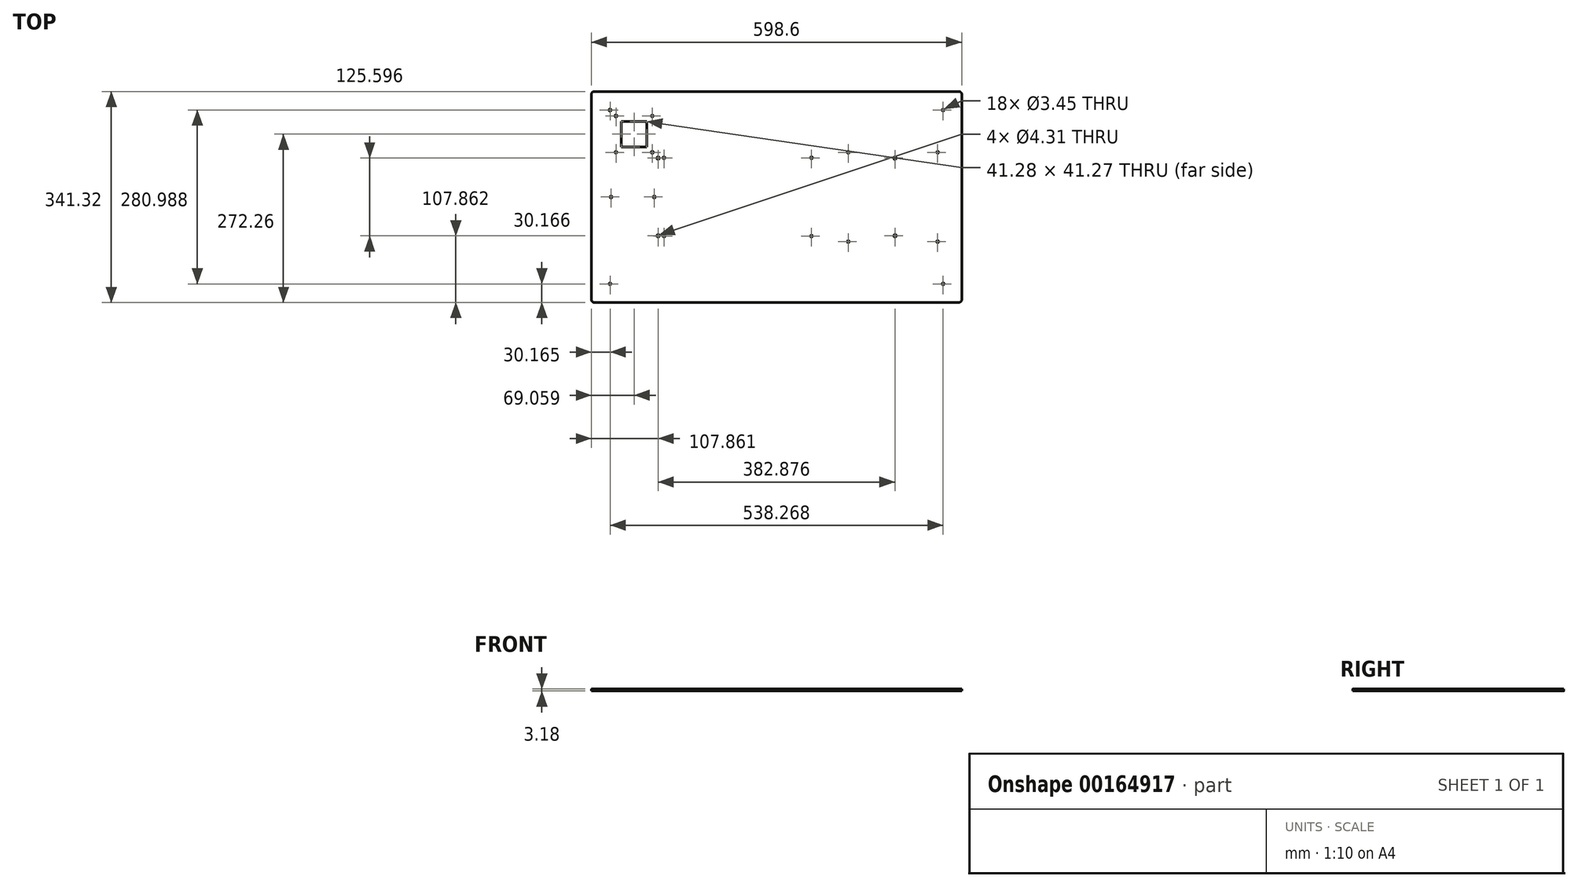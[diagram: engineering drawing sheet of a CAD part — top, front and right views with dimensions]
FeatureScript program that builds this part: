
annotation { "Feature Type Name" : "Feature", "Feature Type Description" : "" }
export const myFeature = defineFeature(function(context is Context, id is Id, definition is map)
    precondition{}
    {
        {
            var Q0;
            Q0=qCreatedBy(makeId("Top.planeOp"),FACE);
            var sketch = newSketch(context, id + "F0", { "sketchPlane" : qUnion([Q0])});
            skPoint(sketch, "E0.middle", {"position": v(0, 0) * mm});
            skLineSegment(sketch, "E1", {"start": v(0, 101.6) * mm, "end": v(0, 0) * mm, "construction": true});
            skLineSegment(sketch, "E2", {"start": v(0, 101.6) * mm, "end": v(-167.48, 101.6) * mm, "construction": true});
            skLineSegment(sketch, "E3.bottom", {"start": v(-138.11, 72.23) * mm, "end": v(-196.85, 72.23) * mm, "construction": true});
            skLineSegment(sketch, "E3.top", {"start": v(-138.11, 130.97) * mm, "end": v(-196.85, 130.97) * mm, "construction": true});
            skLineSegment(sketch, "E3.left", {"start": v(-138.11, 72.23) * mm, "end": v(-138.11, 130.97) * mm, "construction": true});
            skLineSegment(sketch, "E3.right", {"start": v(-196.85, 72.23) * mm, "end": v(-196.85, 130.97) * mm, "construction": true});
            skPoint(sketch, "E3.middle", {"position": v(-167.48, 101.6) * mm});
            skCircle(sketch, "E4", {"center": v(-196.85, 130.97) * mm, "radius": 1.73 * mm});
            skCircle(sketch, "E5", {"center": v(-138.11, 130.97) * mm, "radius": 1.73 * mm});
            skCircle(sketch, "E6", {"center": v(-138.11, 72.23) * mm, "radius": 1.73 * mm});
            skCircle(sketch, "E7", {"center": v(-196.85, 72.23) * mm, "radius": 1.73 * mm});
            skLineSegment(sketch, "E8", {"start": v(0, 0) * mm, "end": v(-119.17, 63.3) * mm, "construction": true});
            skLineSegment(sketch, "E9", {"start": v(0, 0) * mm, "end": v(-119.17, 0) * mm, "construction": true});
            skLineSegment(sketch, "E10", {"start": v(0, 0) * mm, "end": v(119.17, 0) * mm, "construction": true});
            skLineSegment(sketch, "E11", {"start": v(0, 0) * mm, "end": v(-119.17, -63.3) * mm, "construction": true});
            skLineSegment(sketch, "E12", {"start": v(0, 0) * mm, "end": v(119.17, -63.3) * mm, "construction": true});
            skLineSegment(sketch, "E13", {"start": v(0, 0) * mm, "end": v(119.17, 63.3) * mm, "construction": true});
            skLineSegment(sketch, "E14", {"start": v(119.17, -63.3) * mm, "end": v(119.17, 63.3) * mm, "construction": true});
            skLineSegment(sketch, "E15", {"start": v(-119.17, -63.3) * mm, "end": v(-119.17, 63.3) * mm, "construction": true});
            skCircle(sketch, "E16", {"center": v(-119.17, -63.3) * mm, "radius": 1.73 * mm});
            skCircle(sketch, "E17", {"center": v(-119.17, 63.3) * mm, "radius": 1.73 * mm});
            skCircle(sketch, "E18", {"center": v(119.17, -63.3) * mm, "radius": 1.73 * mm});
            skCircle(sketch, "E19", {"center": v(119.17, 63.3) * mm, "radius": 1.73 * mm});
            skCircle(sketch, "E20", {"center": v(-128.68, -62.8) * mm, "radius": 2.15 * mm});
            skCircle(sketch, "E21", {"center": v(-128.68, 62.8) * mm, "radius": 2.15 * mm});
            skCircle(sketch, "E22", {"center": v(254.2, -62.8) * mm, "radius": 2.15 * mm});
            skCircle(sketch, "E23", {"center": v(254.2, 62.8) * mm, "radius": 2.15 * mm});
            skCircle(sketch, "E24", {"center": v(-119.17, -63.3) * mm, "radius": 4.76 * mm, "construction": true});
            skCircle(sketch, "E25", {"center": v(-128.68, -62.8) * mm, "radius": 4.76 * mm, "construction": true});
            skLineSegment(sketch, "E26.bottom", {"start": v(-188.12, 122.24) * mm, "end": v(-146.84, 122.24) * mm});
            skLineSegment(sketch, "E26.top", {"start": v(-188.12, 80.96) * mm, "end": v(-146.84, 80.96) * mm});
            skLineSegment(sketch, "E26.left", {"start": v(-188.12, 122.24) * mm, "end": v(-188.12, 80.96) * mm});
            skLineSegment(sketch, "E26.right", {"start": v(-146.84, 122.24) * mm, "end": v(-146.84, 80.96) * mm});
            skLineSegment(sketch, "E27", {"start": v(-196.85, 130.97) * mm, "end": v(-206.37, 130.97) * mm, "construction": true});
            skLineSegment(sketch, "E28", {"start": v(-196.85, 130.97) * mm, "end": v(-196.85, 140.5) * mm, "construction": true});
            skLineSegment(sketch, "E29.bottom", {"start": v(-236.54, -170.66) * mm, "end": v(362.06, -170.66) * mm});
            skLineSegment(sketch, "E29.top", {"start": v(-236.54, 170.66) * mm, "end": v(362.06, 170.66) * mm});
            skLineSegment(sketch, "E29.left", {"start": v(-236.54, -170.66) * mm, "end": v(-236.54, 170.66) * mm});
            skLineSegment(sketch, "E29.right", {"start": v(362.06, -170.66) * mm, "end": v(362.06, 170.66) * mm});
            skLineSegment(sketch, "E30", {"start": v(-119.17, 0) * mm, "end": v(-236.54, 0) * mm, "construction": true});
            skLineSegment(sketch, "E31", {"start": v(362.06, 0) * mm, "end": v(250.93, 0) * mm, "construction": true});
            skLineSegment(sketch, "E32.bottom", {"start": v(323.16, 72.23) * mm, "end": v(178.7, 72.23) * mm, "construction": true});
            skLineSegment(sketch, "E32.top", {"start": v(323.16, -72.23) * mm, "end": v(178.7, -72.23) * mm, "construction": true});
            skLineSegment(sketch, "E32.left", {"start": v(323.16, 72.23) * mm, "end": v(323.16, -72.23) * mm, "construction": true});
            skLineSegment(sketch, "E32.right", {"start": v(178.7, 72.23) * mm, "end": v(178.7, -72.23) * mm, "construction": true});
            skPoint(sketch, "E32.middle", {"position": v(250.93, 0) * mm});
            skCircle(sketch, "E33", {"center": v(178.7, -72.23) * mm, "radius": 1.73 * mm});
            skCircle(sketch, "E34", {"center": v(178.7, 72.23) * mm, "radius": 1.73 * mm});
            skCircle(sketch, "E35", {"center": v(323.16, 72.23) * mm, "radius": 1.73 * mm});
            skCircle(sketch, "E36", {"center": v(323.16, -72.23) * mm, "radius": 1.73 * mm});
            skLineSegment(sketch, "E37", {"start": v(250.93, 0) * mm, "end": v(119.17, 0) * mm, "construction": true});
            skLineSegment(sketch, "E38.bottom", {"start": v(-128.68, -62.8) * mm, "end": v(254.2, -62.8) * mm, "construction": true});
            skLineSegment(sketch, "E38.top", {"start": v(-128.68, 62.8) * mm, "end": v(254.2, 62.8) * mm, "construction": true});
            skLineSegment(sketch, "E38.left", {"start": v(-128.68, -62.8) * mm, "end": v(-128.68, 62.8) * mm, "construction": true});
            skLineSegment(sketch, "E38.right", {"start": v(254.2, -62.8) * mm, "end": v(254.2, 62.8) * mm, "construction": true});
            skLineSegment(sketch, "E39", {"start": v(62.76, -62.8) * mm, "end": v(62.76, -170.66) * mm, "construction": true});
            skLineSegment(sketch, "E40", {"start": v(62.76, 62.8) * mm, "end": v(62.76, 170.66) * mm, "construction": true});
            skSolve(sketch);
        }
        {
            var Q0;
            Q0=qSketchRegion(id+"F0",true);
            extrude(context, id + "F1", {"entities" : qUnion([Q0]), "depth" : 3.17 * mm});
        }
        {
            var Q0;
            Q0=makeQuery(id+"F1.opExtrude","CAP_FACE",FACE,{"disambiguationData":[OSD([sQuery(id+"F0.wireOp",EDGE,"E0.bottom"),sQuery(id+"F0.wireOp",EDGE,"E0.top"),sQuery(id+"F0.wireOp",EDGE,"E0.left"),sQuery(id+"F0.wireOp",EDGE,"E0.right"),sQuery(id+"F0.wireOp",EDGE,"E4"),sQuery(id+"F0.wireOp",EDGE,"E5"),sQuery(id+"F0.wireOp",EDGE,"E6"),sQuery(id+"F0.wireOp",EDGE,"E7"),sQuery(id+"F0.wireOp",EDGE,"E16"),sQuery(id+"F0.wireOp",EDGE,"E17"),sQuery(id+"F0.wireOp",EDGE,"E18"),sQuery(id+"F0.wireOp",EDGE,"E19"),sQuery(id+"F0.wireOp",EDGE,"E20"),sQuery(id+"F0.wireOp",EDGE,"E21"),sQuery(id+"F0.wireOp",EDGE,"E22"),sQuery(id+"F0.wireOp",EDGE,"E23")])],"isStart":false});
            var sketch = newSketch(context, id + "F2", { "sketchPlane" : qUnion([Q0])});
            skLineSegment(sketch, "E41.bottom", {"start": v(-206.37, 140.5) * mm, "end": v(331.9, 140.5) * mm, "construction": true});
            skLineSegment(sketch, "E41.top", {"start": v(-206.37, -140.5) * mm, "end": v(331.9, -140.5) * mm, "construction": true});
            skLineSegment(sketch, "E41.left", {"start": v(-206.38, 140.5) * mm, "end": v(-206.38, -140.5) * mm, "construction": true});
            skLineSegment(sketch, "E41.right", {"start": v(331.9, 140.5) * mm, "end": v(331.9, -140.5) * mm, "construction": true});
            skPoint(sketch, "E41.middle", {"position": v(62.76, 0) * mm});
            skLineSegment(sketch, "E42.bottom", {"start": v(-206.37, 140.5) * mm, "end": v(-236.54, 140.5) * mm, "construction": true});
            skLineSegment(sketch, "E42.top", {"start": v(-206.37, 170.66) * mm, "end": v(-236.54, 170.66) * mm, "construction": true});
            skLineSegment(sketch, "E42.left", {"start": v(-206.38, 140.5) * mm, "end": v(-206.38, 170.66) * mm, "construction": true});
            skLineSegment(sketch, "E42.right", {"start": v(-236.54, 140.5) * mm, "end": v(-236.54, 170.66) * mm, "construction": true});
            skCircle(sketch, "E43", {"center": v(-206.37, -140.5) * mm, "radius": 1.73 * mm});
            skCircle(sketch, "E44", {"center": v(-206.37, 140.5) * mm, "radius": 1.73 * mm});
            skCircle(sketch, "E45", {"center": v(331.9, 140.5) * mm, "radius": 1.73 * mm});
            skCircle(sketch, "E46", {"center": v(331.9, -140.5) * mm, "radius": 1.73 * mm});
            skLineSegment(sketch, "E47", {"start": v(-196.85, 72.23) * mm, "end": v(-206.38, 72.23) * mm, "construction": true});
            skLineSegment(sketch, "E48", {"start": v(-196.85, 72.23) * mm, "end": v(-196.85, -140.5) * mm, "construction": true});
            skLineSegment(sketch, "E49.bottom", {"start": v(331.9, -140.5) * mm, "end": v(362.06, -140.5) * mm, "construction": true});
            skLineSegment(sketch, "E49.top", {"start": v(331.9, -170.66) * mm, "end": v(362.06, -170.66) * mm, "construction": true});
            skLineSegment(sketch, "E49.left", {"start": v(331.9, -140.5) * mm, "end": v(331.9, -170.66) * mm, "construction": true});
            skLineSegment(sketch, "E49.right", {"start": v(362.06, -140.5) * mm, "end": v(362.06, -170.66) * mm, "construction": true});
            skSolve(sketch);
        }
        {
            var Q0;
            Q0=makeQuery(id+"F1.opExtrude","SWEPT_EDGE",EDGE,{"disambiguationData":[OSD([sQuery(id+"F0.wireOp",EDGE,"E29.bottom"),sQuery(id+"F0.wireOp",EDGE,"E29.right")])]});
            var Q1;
            Q1=makeQuery(id+"F1.opExtrude","SWEPT_EDGE",EDGE,{"disambiguationData":[OSD([sQuery(id+"F0.wireOp",EDGE,"E29.bottom"),sQuery(id+"F0.wireOp",EDGE,"E29.left")])]});
            var Q2;
            Q2=makeQuery(id+"F1.opExtrude","SWEPT_EDGE",EDGE,{"disambiguationData":[OSD([sQuery(id+"F0.wireOp",EDGE,"E29.top"),sQuery(id+"F0.wireOp",EDGE,"E29.left")])]});
            var Q3;
            Q3=makeQuery(id+"F1.opExtrude","SWEPT_EDGE",EDGE,{"disambiguationData":[OSD([sQuery(id+"F0.wireOp",EDGE,"E29.top"),sQuery(id+"F0.wireOp",EDGE,"E29.right")])]});
            fillet(context, id + "F3", {"entities" : qUnion([Q0, Q1, Q2, Q3]), "radius" : 4.76 * mm, "tangentPropagation" : true, "allowEdgeOverflow" : false});
        }
        {
            var Q0;
            Q0=qSketchRegion(id+"F2",true);
            var Q1;
            Q1=makeQuery(id+"F1.opExtrude","CAP_FACE",FACE,{"disambiguationData":[OSD([sQuery(id+"F0.wireOp",EDGE,"E0.bottom"),sQuery(id+"F0.wireOp",EDGE,"E0.top"),sQuery(id+"F0.wireOp",EDGE,"E0.left"),sQuery(id+"F0.wireOp",EDGE,"E0.right"),sQuery(id+"F0.wireOp",EDGE,"E4"),sQuery(id+"F0.wireOp",EDGE,"E5"),sQuery(id+"F0.wireOp",EDGE,"E6"),sQuery(id+"F0.wireOp",EDGE,"E7"),sQuery(id+"F0.wireOp",EDGE,"E16"),sQuery(id+"F0.wireOp",EDGE,"E17"),sQuery(id+"F0.wireOp",EDGE,"E18"),sQuery(id+"F0.wireOp",EDGE,"E19"),sQuery(id+"F0.wireOp",EDGE,"E20"),sQuery(id+"F0.wireOp",EDGE,"E21"),sQuery(id+"F0.wireOp",EDGE,"E22"),sQuery(id+"F0.wireOp",EDGE,"E23")])],"isStart":true});
            extrude(context, id + "F4", {"entities" : qUnion([Q0]), "operationType" : NewBodyOperationType.REMOVE, "endBound" : BoundingType.UP_TO_SURFACE, "oppositeDirection" : true, "endBoundEntityFace" : qUnion([Q1]), "depth" : 25.4 * mm});
        }
        {
            var Q0;
            Q0=makeQuery(id+"F1.opExtrude","CAP_FACE",FACE,{"disambiguationData":[OSD([sQuery(id+"F0.wireOp",EDGE,"E0.bottom"),sQuery(id+"F0.wireOp",EDGE,"E0.top"),sQuery(id+"F0.wireOp",EDGE,"E0.left"),sQuery(id+"F0.wireOp",EDGE,"E0.right"),sQuery(id+"F0.wireOp",EDGE,"E4"),sQuery(id+"F0.wireOp",EDGE,"E5"),sQuery(id+"F0.wireOp",EDGE,"E6"),sQuery(id+"F0.wireOp",EDGE,"E7"),sQuery(id+"F0.wireOp",EDGE,"E16"),sQuery(id+"F0.wireOp",EDGE,"E17"),sQuery(id+"F0.wireOp",EDGE,"E18"),sQuery(id+"F0.wireOp",EDGE,"E19"),sQuery(id+"F0.wireOp",EDGE,"E20"),sQuery(id+"F0.wireOp",EDGE,"E21"),sQuery(id+"F0.wireOp",EDGE,"E22"),sQuery(id+"F0.wireOp",EDGE,"E23"),sQuery(id+"F0.wireOp",EDGE,"E26.bottom"),sQuery(id+"F0.wireOp",EDGE,"E26.top"),sQuery(id+"F0.wireOp",EDGE,"E26.left"),sQuery(id+"F0.wireOp",EDGE,"E26.right")])],"isStart":false});
            var sketch = newSketch(context, id + "F5", { "sketchPlane" : qUnion([Q0])});
            skLineSegment(sketch, "E50", {"start": v(-236.54, 0) * mm, "end": v(-204.79, 0) * mm, "construction": true});
            skLineSegment(sketch, "E51", {"start": v(-204.79, 0) * mm, "end": v(-134.94, 0) * mm, "construction": true});
            skLineSegment(sketch, "E52", {"start": v(-119.17, 63.3) * mm, "end": v(-119.17, -63.3) * mm, "construction": true});
            skLineSegment(sketch, "E53", {"start": v(-119.17, 0) * mm, "end": v(-134.94, 0) * mm, "construction": true});
            skCircle(sketch, "E54", {"center": v(-134.94, 0) * mm, "radius": 1.73 * mm});
            skCircle(sketch, "E55", {"center": v(-204.79, 0) * mm, "radius": 1.73 * mm});
            skSolve(sketch);
        }
        {
            var Q0;
            Q0=qSketchRegion(id+"F5",true);
            var Q1;
            Q1=makeQuery(id+"F1.opExtrude","CAP_FACE",FACE,{"disambiguationData":[OSD([sQuery(id+"F0.wireOp",EDGE,"E0.bottom"),sQuery(id+"F0.wireOp",EDGE,"E0.top"),sQuery(id+"F0.wireOp",EDGE,"E0.left"),sQuery(id+"F0.wireOp",EDGE,"E0.right"),sQuery(id+"F0.wireOp",EDGE,"E4"),sQuery(id+"F0.wireOp",EDGE,"E5"),sQuery(id+"F0.wireOp",EDGE,"E6"),sQuery(id+"F0.wireOp",EDGE,"E7"),sQuery(id+"F0.wireOp",EDGE,"E16"),sQuery(id+"F0.wireOp",EDGE,"E17"),sQuery(id+"F0.wireOp",EDGE,"E18"),sQuery(id+"F0.wireOp",EDGE,"E19"),sQuery(id+"F0.wireOp",EDGE,"E20"),sQuery(id+"F0.wireOp",EDGE,"E21"),sQuery(id+"F0.wireOp",EDGE,"E22"),sQuery(id+"F0.wireOp",EDGE,"E23"),sQuery(id+"F0.wireOp",EDGE,"E26.bottom"),sQuery(id+"F0.wireOp",EDGE,"E26.top"),sQuery(id+"F0.wireOp",EDGE,"E26.left"),sQuery(id+"F0.wireOp",EDGE,"E26.right")])],"isStart":true});
            extrude(context, id + "F6", {"entities" : qUnion([Q0]), "operationType" : NewBodyOperationType.REMOVE, "endBound" : BoundingType.UP_TO_SURFACE, "oppositeDirection" : true, "endBoundEntityFace" : qUnion([Q1]), "depth" : 25.4 * mm});
        }
    });
